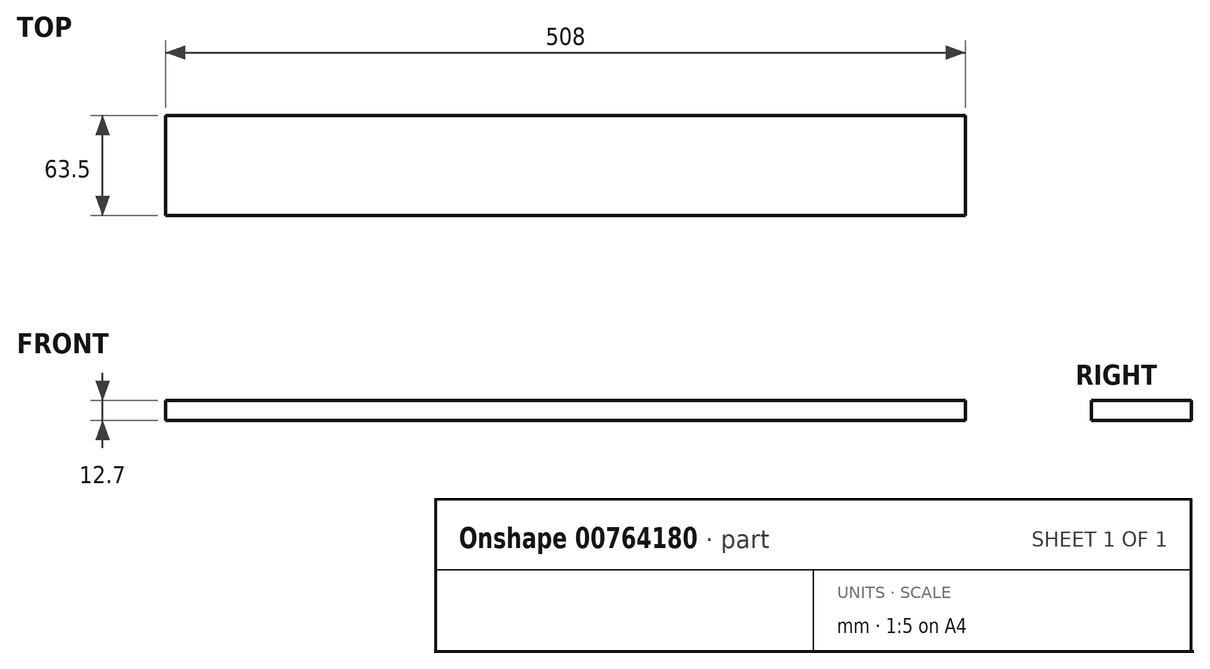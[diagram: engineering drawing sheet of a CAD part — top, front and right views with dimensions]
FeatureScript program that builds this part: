
annotation { "Feature Type Name" : "Feature", "Feature Type Description" : "" }
export const myFeature = defineFeature(function(context is Context, id is Id, definition is map)
    precondition{}
    {
        {
            var Q0;
            Q0=qCreatedBy(makeId("Right.planeOp"),FACE);
            var sketch = newSketch(context, id + "F0", { "sketchPlane" : qUnion([Q0])});
            skLineSegment(sketch, "E0.bottom", {"start": v(0, 0) * mm, "end": v(63.5, 0) * mm});
            skLineSegment(sketch, "E0.top", {"start": v(0, 12.7) * mm, "end": v(63.5, 12.7) * mm});
            skLineSegment(sketch, "E0.left", {"start": v(0, 0) * mm, "end": v(0, 12.7) * mm});
            skLineSegment(sketch, "E0.right", {"start": v(63.5, 0) * mm, "end": v(63.5, 12.7) * mm});
            skSolve(sketch);
        }
        {
            var Q0;
            Q0=makeQuery(id+"F0.imprint","IMPRINT",FACE,{"disambiguationData":[TD([[makeQuery(id+"F0.imprint","IMPRINT",EDGE,{"derivedFrom":sQuery(id+"F0.wireOp",EDGE,"E0.bottom")}),1.0]])]});
            extrude(context, id + "F1", {"entities" : qUnion([Q0]), "oppositeDirection" : true, "depth" : 508 * mm, "offsetDistance" : 25.4 * mm});
        }
    });
